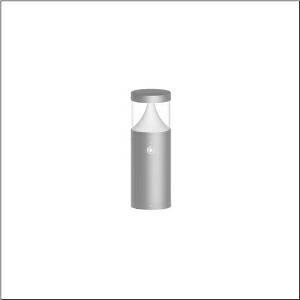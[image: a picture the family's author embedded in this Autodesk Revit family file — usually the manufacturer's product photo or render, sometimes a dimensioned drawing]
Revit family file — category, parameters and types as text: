
# Revit family: cl_31_poller_40_sensor_5cl424803
name_source: partatom
category: Lighting Fixtures
units: mm (PartAtom-declared; Revit-internal decimal feet)

## family parameters
Cut with Voids When Loaded = No
Host = Face
Light Source = No
Part Type = Normal
Room Calculation Point = No
Round Connector Dimension = Use Diameter
Shared = No

## types (1)
- --- (1 x LED, 800 lm, 7.2 W, 3000K)
    Apparent Load = 7 VA
    CIE Flux Codes = 19 66 88 92 100
    Color Rendering = 80
    Color Temperature = 3000K
    Default Elevation = 1800 mm
    Description = CL 31 Bollard 40 Sensor, bollard luminaire, primary light control with lens, of PC, primary optical cover: cover panel, of PC, transparent, secondary light control with reflector, of PC, primary light characteristic: asymmetric, LED, rated luminous flux: 800lm, luminous efficacy: 110lm/W, light colour: 830, colour temperature: 3000K, control gear: DALI, with terminal, 5-pole, max. 2.5mm², mains connection: 220..240V, AC, 50/60Hz, rated input power: 7.2W, luminaire housing, of aluminium, powder-coated, Siteco® metallic grey, diameter: 170mm, height: 400mm, PIR sensor, protection rating (complete): IP65, insulation class (complete): insulation class I (protective earthing), certification: CE, ENEC, impact resistance: IK08, permissible operating ambient temperature for outdoor applications: -20..+50°C, packaging unit: 1 piece
    Height = 200 mm  [stored 0.656168 ft]
    Lamp = 1 x LED
    Lamp Light Flux = 800 lm
    Lamp Power = 7.2 W
    Lamp count = 1
    Length = 170 mm  [stored 0.557743 ft]
    Luminous efficacy = 111 lm/W
    Manufacturer = Siteco
    ModVariant = No
    Model = 5CL424803
    Mounting Place = Floor
    Mounting Type = Freestanding
    Number of Poles = 1
    OnlyDefault = Yes
    Power Factor = 1
    Product Name = CL 31 Poller 40 Sensor
    Product group = bollard luminaire
    ProductGroupID = 1304
    Protection Class = Protection class I
    Protection Degree = IP 65
    RLX_Detail_Level = 1
    RLX_Emergency_Light_Flux = 0 lm
    RLX_Emergency_Type = 0
    RLX_Emergency_Type_DB = No
    RlxData = <blob elided: 62661 chars, md5=be621314>
    Socket = socket
    Standby Power = 0 W
    System Light Flux = 800 lm
    System Power = 7 W
    Type Comments = factory setting: luminous flux: 100 % | dim-lin: 254 | 182 mA
    Type Image = l_1006905.jpg
    URL = http://relux.com
    VarID = @adj_216501
    Voltage = 0 V
    Weight = 0.00 kg
    Width = 0 mm  [stored 0 ft]

note: [stored X ft] marks values corroborated as IEEE doubles in the binary element streams (Revit-internal decimal feet)

## geometry (parser evidence)
native form markers: Blend x4, Sweep x12
no freeform markers — native parametric forms only
